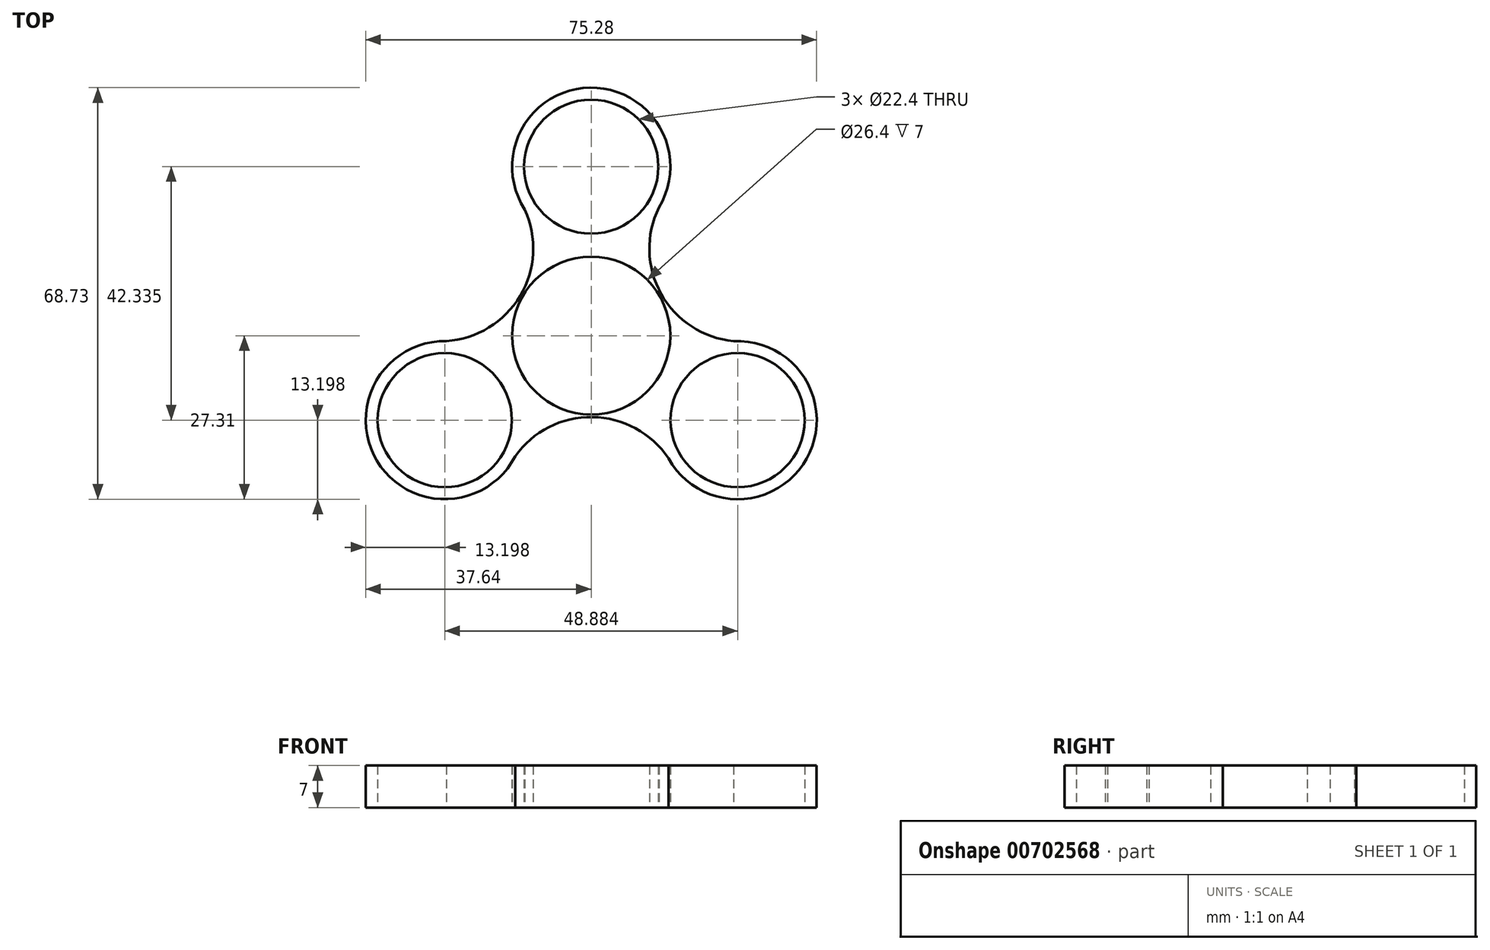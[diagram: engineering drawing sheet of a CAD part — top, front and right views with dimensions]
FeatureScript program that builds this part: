
annotation { "Feature Type Name" : "Feature", "Feature Type Description" : "" }
export const myFeature = defineFeature(function(context is Context, id is Id, definition is map)
    precondition{}
    {
        {
            var Q0;
            Q0=qCreatedBy(makeId("Top.planeOp"),FACE);
            var sketch = newSketch(context, id + "F0", { "sketchPlane" : qUnion([Q0])});
            skCircle(sketch, "E0", {"center": v(0, 0) * mm, "radius": 11.2 * mm});
            skCircle(sketch, "E1", {"center": v(0, 0) * mm, "radius": 13.2 * mm});
            skCircle(sketch, "E2", {"center": v(0, 28.22) * mm, "radius": 11.2 * mm});
            skArc(sketch, "E3", {"start": v(11.3, 21.41) * mm, "mid": v(-0.2, 41.42) * mm, "end": v(-11.1, 21.06) * mm});
            skCircle(sketch, "E4.1.0", {"center": v(-24.44, -14.11) * mm, "radius": 11.2 * mm});
            skArc(sketch, "E4.1.1", {"start": v(-24.2, -0.91) * mm, "mid": v(-35.77, -20.89) * mm, "end": v(-12.7, -20.14) * mm});
            skCircle(sketch, "E4.2.0", {"center": v(24.44, -14.11) * mm, "radius": 11.2 * mm});
            skArc(sketch, "E4.2.1", {"start": v(12.9, -20.5) * mm, "mid": v(35.98, -20.53) * mm, "end": v(23.79, -0.93) * mm});
            skArc(sketch, "E5", {"start": v(11.3, 21.41) * mm, "mid": v(11.68, 6.96) * mm, "end": v(23.79, -0.93) * mm});
            skArc(sketch, "E6.1.0", {"start": v(-24.2, -0.91) * mm, "mid": v(-11.87, 6.63) * mm, "end": v(-11.1, 21.06) * mm});
            skArc(sketch, "E6.2.0", {"start": v(12.9, -20.5) * mm, "mid": v(0.2, -13.6) * mm, "end": v(-12.7, -20.14) * mm});
            skSolve(sketch);
        }
        {
            var Q0;
            Q0 = qSketchRegion(id + "F0", true);
            extrude(context, id + "F1", {"entities" : qUnion([Q0]), "depth" : 7 * mm, "offsetDistance" : 25 * mm});
        }
    });
